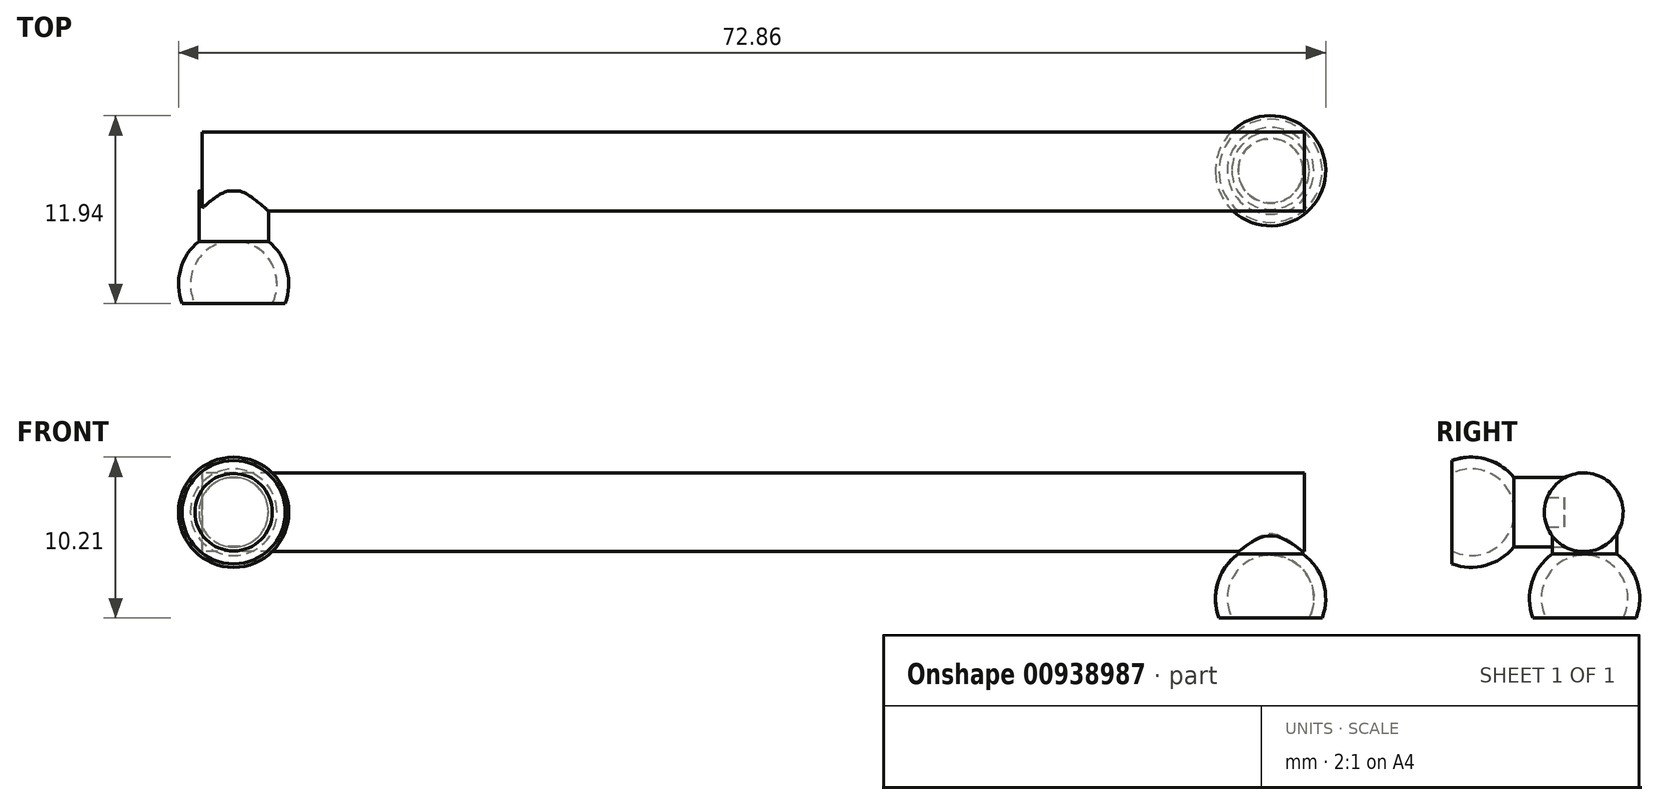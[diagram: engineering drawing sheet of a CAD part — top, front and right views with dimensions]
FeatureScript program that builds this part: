
annotation { "Feature Type Name" : "Feature", "Feature Type Description" : "" }
export const myFeature = defineFeature(function(context is Context, id is Id, definition is map)
    precondition{}
    {
        {
            var Q0;
            Q0=qCreatedBy(makeId("Top.planeOp"),FACE);
            var sketch = newSketch(context, id + "F0", { "sketchPlane" : qUnion([Q0])});
            skLineSegment(sketch, "E0", {"start": v(3, 0) * mm, "end": v(3, -3.02) * mm});
            skArc(sketch, "E1", {"start": v(5.46, -1.24) * mm, "mid": v(5.34, 1.44) * mm, "end": v(3, 2.75) * mm});
            skArc(sketch, "E2", {"start": v(6.27, -1.24) * mm, "mid": v(5.88, 2) * mm, "end": v(3, 3.5) * mm});
            skLineSegment(sketch, "E3.trimOffspring", {"start": v(5.46, -1.24) * mm, "end": v(6.27, -1.24) * mm});
            skLineSegment(sketch, "E4", {"start": v(3, 0) * mm, "end": v(3, 3.5) * mm});
            skLineSegment(sketch, "E5", {"start": v(3, 3.5) * mm, "end": v(3, 5.91) * mm});
            skLineSegment(sketch, "E6", {"start": v(3, 5.91) * mm, "end": v(5.2, 5.91) * mm});
            skLineSegment(sketch, "E7", {"start": v(5.2, 5.91) * mm, "end": v(5.2, 2.72) * mm});
            skSolve(sketch);
        }
        {
            var Q0;
            {var subQ5=sQuery(id+"F0.wireOp",EDGE,"E1");Q0=makeQuery(id+"F0.imprint","IMPRINT",FACE,{"disambiguationData":[TD([[makeQuery(id+"F0.imprint","IMPRINT",EDGE,{"derivedFrom":subQ5}),-1.0]])]});}
            var Q1;
            {var subQ0=sQuery(id+"F0.wireOp",EDGE,"E5");Q1=makeQuery(id+"F0.imprint","IMPRINT",FACE,{"disambiguationData":[TD([[makeQuery(id+"F0.imprint","IMPRINT",EDGE,{"derivedFrom":subQ0}),-1.0]])]});}
            var Q2;
            Q2=sQuery(id+"F0.wireOp",EDGE,"E0");
            revolve(context, id + "F1", {"surfaceOperationType" : NewSurfaceOperationType.NEW, "entities" : qUnion([Q0, Q1]), "axis" : qUnion([Q2]), "revolveType" : RevolveType.FULL});
        }
        {
            var Q0;
            Q0=qCreatedBy(makeId("Right.planeOp"),FACE);
            cPlane(context, id + "F2", {"entities" : qUnion([Q0]), "cplaneType" : CPlaneType.OFFSET, "offset" : 36 * mm, "width" : 150 * mm, "height" : 150 * mm});
        }
        {
            var Q0;
            Q0=qCreatedBy(id+"F2.planeOp",FACE);
            var sketch = newSketch(context, id + "F3", { "sketchPlane" : qUnion([Q0])});
            skCircle(sketch, "E8", {"center": v(7.15, 0) * mm, "radius": 2.5 * mm});
            skSolve(sketch);
        }
        {
            var Q0;
            Q0=makeQuery(id+"F3.imprint","IMPRINT",FACE,{"disambiguationData":[TD([[makeQuery(id+"F3.imprint","IMPRINT",EDGE,{"derivedFrom":sQuery(id+"F3.wireOp",EDGE,"E8")}),1.0]])]});
            extrude(context, id + "F4", {"entities" : qUnion([Q0]), "operationType" : NewBodyOperationType.ADD, "depth" : 70 * mm, "offsetDistance" : 25 * mm, "symmetric" : true});
        }
        {
            var Q0;
            Q0=makeQuery(id+"F1.opRevolve","SWEPT_BODY",BODY,{"disambiguationData":[OSD([sQuery(id+"F0.wireOp",EDGE,"E1"),sQuery(id+"F0.wireOp",EDGE,"E2"),sQuery(id+"F0.wireOp",EDGE,"E3.trimOffspring"),sQuery(id+"F0.wireOp",EDGE,"E4"),sQuery(id+"F0.wireOp",EDGE,"E5"),sQuery(id+"F0.wireOp",EDGE,"E6"),sQuery(id+"F0.wireOp",EDGE,"E7")])]});
            transform(context, id + "F5", {"entities" : qUnion([Q0]), "transformType" : TransformType.TRANSLATION_3D, "dx" : 0 * mm, "dy" : -7.2 * mm, "dz" : 0 * mm, "makeCopy" : false});
        }
        {
            var Q0;
            Q0=qCreatedBy(makeId("Front.planeOp"),FACE);
            var sketch = newSketch(context, id + "F6", { "sketchPlane" : qUnion([Q0])});
            skLineSegment(sketch, "E9", {"start": v(68.86, -5.48) * mm, "end": v(68.86, -8.5) * mm});
            skArc(sketch, "E10", {"start": v(71.32, -6.71) * mm, "mid": v(71.2, -4.03) * mm, "end": v(68.86, -2.73) * mm});
            skArc(sketch, "E11", {"start": v(72.13, -6.71) * mm, "mid": v(71.74, -3.49) * mm, "end": v(68.86, -1.98) * mm});
            skLineSegment(sketch, "E12.trimOffspring", {"start": v(71.32, -6.71) * mm, "end": v(72.13, -6.71) * mm});
            skLineSegment(sketch, "E13", {"start": v(68.86, -5.48) * mm, "end": v(68.86, -1.98) * mm});
            skLineSegment(sketch, "E14", {"start": v(68.86, -1.98) * mm, "end": v(68.86, 0.43) * mm});
            skLineSegment(sketch, "E15", {"start": v(68.86, 0.43) * mm, "end": v(70.92, 0.43) * mm});
            skLineSegment(sketch, "E16", {"start": v(70.92, 0.43) * mm, "end": v(70.92, -2.65) * mm});
            skSolve(sketch);
        }
        {
            var Q0;
            {var subQ5=sQuery(id+"F6.wireOp",EDGE,"E10");Q0=makeQuery(id+"F6.imprint","IMPRINT",FACE,{"disambiguationData":[TD([[makeQuery(id+"F6.imprint","IMPRINT",EDGE,{"derivedFrom":subQ5}),-1.0]])]});}
            var Q1;
            {var subQ0=sQuery(id+"F6.wireOp",EDGE,"E14");Q1=makeQuery(id+"F6.imprint","IMPRINT",FACE,{"disambiguationData":[TD([[makeQuery(id+"F6.imprint","IMPRINT",EDGE,{"derivedFrom":subQ0}),-1.0]])]});}
            var Q2;
            Q2=sQuery(id+"F6.wireOp",EDGE,"E13");
            revolve(context, id + "F7", {"operationType" : NewBodyOperationType.ADD, "surfaceOperationType" : NewSurfaceOperationType.NEW, "entities" : qUnion([Q0, Q1]), "axis" : qUnion([Q2]), "revolveType" : RevolveType.FULL});
        }
    });
